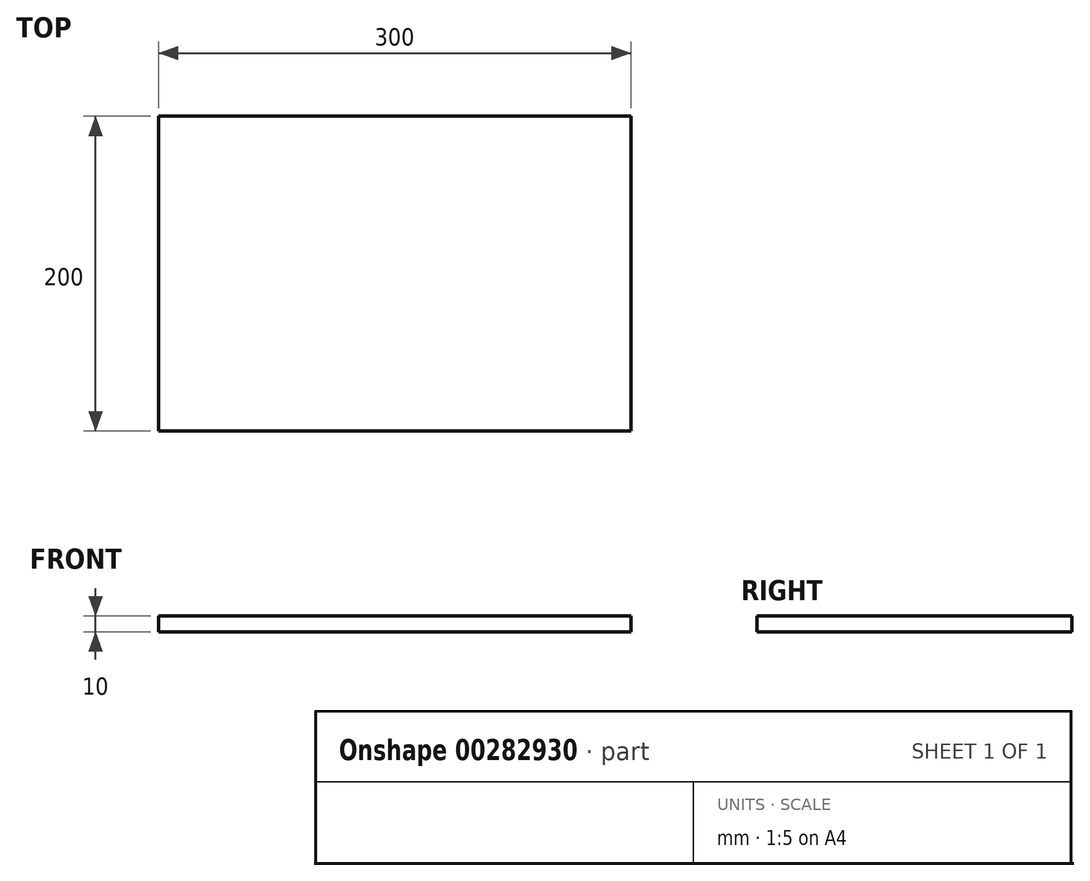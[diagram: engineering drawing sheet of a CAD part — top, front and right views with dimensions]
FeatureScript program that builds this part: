
annotation { "Feature Type Name" : "Feature", "Feature Type Description" : "" }
export const myFeature = defineFeature(function(context is Context, id is Id, definition is map)
    precondition{}
    {
        {
            var Q0;
            Q0=qCreatedBy(makeId("Top.planeOp"),FACE);
            var sketch = newSketch(context, id + "F0", { "sketchPlane" : qUnion([Q0])});
            skLineSegment(sketch, "E0.bottom", {"start": v(150, 100) * mm, "end": v(-150, 100) * mm});
            skLineSegment(sketch, "E0.top", {"start": v(150, -100) * mm, "end": v(-150, -100) * mm});
            skLineSegment(sketch, "E0.left", {"start": v(150, 100) * mm, "end": v(150, -100) * mm});
            skLineSegment(sketch, "E0.right", {"start": v(-150, 100) * mm, "end": v(-150, -100) * mm});
            skPoint(sketch, "E0.middle", {"position": v(0, 0) * mm});
            skSolve(sketch);
        }
        {
            var Q0;
            Q0=makeQuery(id+"F0.imprint","IMPRINT",FACE,{"disambiguationData":[TD([[makeQuery(id+"F0.imprint","IMPRINT",EDGE,{"derivedFrom":sQuery(id+"F0.wireOp",EDGE,"E0.bottom")}),1.0]])]});
            extrude(context, id + "F1", {"entities" : qUnion([Q0]), "depth" : 10 * mm});
        }
    });
